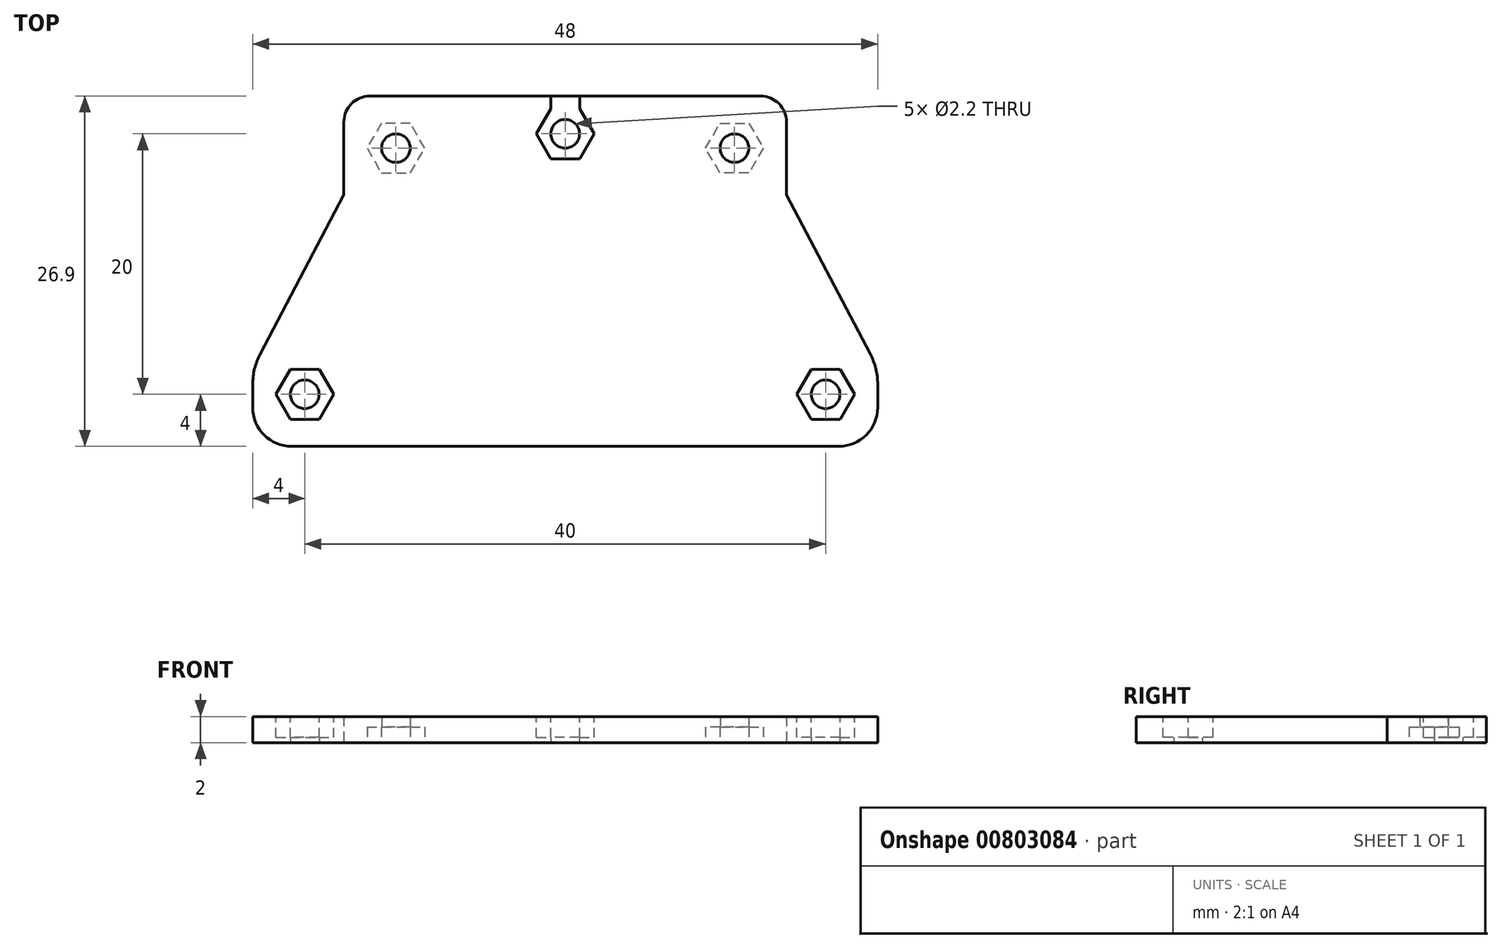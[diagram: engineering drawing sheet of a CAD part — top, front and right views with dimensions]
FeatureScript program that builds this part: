
annotation { "Feature Type Name" : "Feature", "Feature Type Description" : "" }
export const myFeature = defineFeature(function(context is Context, id is Id, definition is map)
    precondition{}
    {
        {
            var Q0;
            Q0=qCreatedBy(makeId("Top.planeOp"),FACE);
            var sketch = newSketch(context, id + "F0", { "sketchPlane" : qUnion([Q0])});
            skCircle(sketch, "E0", {"center": v(-13, 0) * mm, "radius": 1.1 * mm});
            skCircle(sketch, "E1", {"center": v(0, 1.1) * mm, "radius": 1.1 * mm});
            skCircle(sketch, "E2", {"center": v(-20, -18.9) * mm, "radius": 1.1 * mm});
            skCircle(sketch, "E3.MirrorC", {"center": v(20, -18.9) * mm, "radius": 1.1 * mm});
            skCircle(sketch, "E4.MirrorC", {"center": v(13, 0) * mm, "radius": 1.1 * mm});
            skLineSegment(sketch, "E5", {"start": v(-14.82, 3.1) * mm, "end": v(20.83, 3.1) * mm, "construction": true});
            skSolve(sketch);
        }
        {
            var Q0;
            Q0=qCreatedBy(makeId("Top.planeOp"),FACE);
            var sketch = newSketch(context, id + "F1", { "sketchPlane" : qUnion([Q0])});
            skLineSegment(sketch, "E6", {"start": v(-3, 4) * mm, "end": v(-13, 4) * mm});
            skLineSegment(sketch, "E7", {"start": v(-17, -3.6) * mm, "end": v(-24, -16.9) * mm});
            skLineSegment(sketch, "E8", {"start": v(-24, -22.9) * mm, "end": v(0, -22.9) * mm});
            skLineSegment(sketch, "E9", {"start": v(-3, 4) * mm, "end": v(0, 4) * mm});
            skLineSegment(sketch, "E10", {"start": v(-13, 4) * mm, "end": v(-17, 4) * mm});
            skLineSegment(sketch, "E11", {"start": v(-17, 4) * mm, "end": v(-17, -3.6) * mm});
            skLineSegment(sketch, "E12", {"start": v(-24, -16.9) * mm, "end": v(-24, -22.9) * mm});
            skLineSegment(sketch, "E13.MirrorCS", {"start": v(24, -22.9) * mm, "end": v(0, -22.9) * mm});
            skLineSegment(sketch, "E14.MirrorCS", {"start": v(17, -3.6) * mm, "end": v(24, -16.9) * mm});
            skLineSegment(sketch, "E15.MirrorCS", {"start": v(24, -16.9) * mm, "end": v(24, -22.9) * mm});
            skLineSegment(sketch, "E16.MirrorCS", {"start": v(3, 4) * mm, "end": v(0, 4) * mm});
            skLineSegment(sketch, "E17.MirrorCS", {"start": v(13, 4) * mm, "end": v(17, 4) * mm});
            skLineSegment(sketch, "E18.MirrorCS", {"start": v(3, 4) * mm, "end": v(13, 4) * mm});
            skLineSegment(sketch, "E19.MirrorCS", {"start": v(17, 4) * mm, "end": v(17, -3.6) * mm});
            skSolve(sketch);
        }
        {
            var Q0;
            Q0=qSketchRegion(id+"F1",true);
            extrude(context, id + "F2", {"entities" : qUnion([Q0]), "depth" : 2 * mm, "offsetDistance" : 25 * mm});
        }
        {
            var Q0;
            Q0=makeQuery(id+"F2.opExtrude","CAP_FACE",FACE,{"disambiguationData":[OSD([sQuery(id+"F1.wireOp",EDGE,"E6"),sQuery(id+"F1.wireOp",EDGE,"E7"),sQuery(id+"F1.wireOp",EDGE,"E8"),sQuery(id+"F1.wireOp",EDGE,"E9"),sQuery(id+"F1.wireOp",EDGE,"E10"),sQuery(id+"F1.wireOp",EDGE,"E11"),sQuery(id+"F1.wireOp",EDGE,"E12"),sQuery(id+"F1.wireOp",EDGE,"E13.MirrorCS"),sQuery(id+"F1.wireOp",EDGE,"E14.MirrorCS"),sQuery(id+"F1.wireOp",EDGE,"E15.MirrorCS"),sQuery(id+"F1.wireOp",EDGE,"E16.MirrorCS"),sQuery(id+"F1.wireOp",EDGE,"E17.MirrorCS"),sQuery(id+"F1.wireOp",EDGE,"E18.MirrorCS"),sQuery(id+"F1.wireOp",EDGE,"E19.MirrorCS")])],"isStart":true});
            var sketch = newSketch(context, id + "F3", { "sketchPlane" : qUnion([Q0])});
            skCircle(sketch, "E20", {"center": v(20, 18.9) * mm, "radius": 1.1 * mm});
            skCircle(sketch, "E21", {"center": v(13, 0) * mm, "radius": 1.1 * mm});
            skCircle(sketch, "E22", {"center": v(0, -1.1) * mm, "radius": 1.1 * mm});
            skCircle(sketch, "E23", {"center": v(-13, 0) * mm, "radius": 1.1 * mm});
            skCircle(sketch, "E24", {"center": v(-20, 18.9) * mm, "radius": 1.1 * mm});
            skSolve(sketch);
        }
        {
            var Q0;
            Q0=qSketchRegion(id+"F3",true);
            extrude(context, id + "F4", {"entities" : qUnion([Q0]), "operationType" : NewBodyOperationType.REMOVE, "endBound" : BoundingType.UP_TO_NEXT, "oppositeDirection" : true, "depth" : 25 * mm, "offsetDistance" : 25 * mm});
        }
        {
            var Q0;
            Q0=qCreatedBy(makeId("Top.planeOp"),FACE);
            var sketch = newSketch(context, id + "F5", { "sketchPlane" : qUnion([Q0])});
            skCircle(sketch, "E25.cCircle", {"center": v(13, 0) * mm, "radius": 1.92 * mm, "construction": true});
            skLineSegment(sketch, "E25.0", {"start": v(11.9, -1.92) * mm, "end": v(10.78, 0) * mm});
            skLineSegment(sketch, "E25.1", {"start": v(10.78, 0) * mm, "end": v(11.9, 1.92) * mm});
            skLineSegment(sketch, "E25.2", {"start": v(11.9, 1.92) * mm, "end": v(14.1, 1.92) * mm});
            skLineSegment(sketch, "E25.3", {"start": v(14.1, 1.92) * mm, "end": v(15.22, 0) * mm});
            skLineSegment(sketch, "E25.4", {"start": v(15.22, 0) * mm, "end": v(14.1, -1.92) * mm});
            skLineSegment(sketch, "E25.5", {"start": v(14.1, -1.92) * mm, "end": v(11.9, -1.92) * mm});
            skPoint(sketch, "E25.0.midPoint", {"position": v(11.34, -0.96) * mm});
            skLineSegment(sketch, "E26.MirrorCS", {"start": v(-11.9, -1.92) * mm, "end": v(-10.78, 0) * mm});
            skLineSegment(sketch, "E27.MirrorCS", {"start": v(-14.1, 1.92) * mm, "end": v(-15.22, 0) * mm});
            skPoint(sketch, "E28.MirrorP", {"position": v(-11.34, -0.96) * mm});
            skCircle(sketch, "E29.MirrorC", {"center": v(-13, 0) * mm, "radius": 1.92 * mm, "construction": true});
            skLineSegment(sketch, "E30.MirrorCS", {"start": v(-10.78, 0) * mm, "end": v(-11.9, 1.92) * mm});
            skLineSegment(sketch, "E31.MirrorCS", {"start": v(-11.9, 1.92) * mm, "end": v(-14.1, 1.92) * mm});
            skLineSegment(sketch, "E32.MirrorCS", {"start": v(-15.22, 0) * mm, "end": v(-14.1, -1.92) * mm});
            skLineSegment(sketch, "E33.MirrorCS", {"start": v(-14.1, -1.92) * mm, "end": v(-11.9, -1.92) * mm});
            skSolve(sketch);
        }
        {
            var Q0;
            Q0=qSketchRegion(id+"F5",true);
            extrude(context, id + "F6", {"entities" : qUnion([Q0]), "operationType" : NewBodyOperationType.REMOVE, "depth" : 1.2 * mm, "offsetDistance" : 25 * mm});
        }
        {
            var Q0;
            Q0=makeQuery(id+"F2.opExtrude","CAP_FACE",FACE,{"disambiguationData":[OSD([sQuery(id+"F1.wireOp",EDGE,"E6"),sQuery(id+"F1.wireOp",EDGE,"E7"),sQuery(id+"F1.wireOp",EDGE,"E8"),sQuery(id+"F1.wireOp",EDGE,"E9"),sQuery(id+"F1.wireOp",EDGE,"E10"),sQuery(id+"F1.wireOp",EDGE,"E11"),sQuery(id+"F1.wireOp",EDGE,"E12"),sQuery(id+"F1.wireOp",EDGE,"E13.MirrorCS"),sQuery(id+"F1.wireOp",EDGE,"E14.MirrorCS"),sQuery(id+"F1.wireOp",EDGE,"E15.MirrorCS"),sQuery(id+"F1.wireOp",EDGE,"E16.MirrorCS"),sQuery(id+"F1.wireOp",EDGE,"E17.MirrorCS"),sQuery(id+"F1.wireOp",EDGE,"E18.MirrorCS"),sQuery(id+"F1.wireOp",EDGE,"E19.MirrorCS")])],"isStart":false});
            var sketch = newSketch(context, id + "F7", { "sketchPlane" : qUnion([Q0])});
            skCircle(sketch, "E34.cCircle", {"center": v(-20, -18.9) * mm, "radius": 1.92 * mm, "construction": true});
            skLineSegment(sketch, "E34.0", {"start": v(-18.9, -16.98) * mm, "end": v(-17.78, -18.9) * mm});
            skLineSegment(sketch, "E34.1", {"start": v(-17.78, -18.9) * mm, "end": v(-18.9, -20.82) * mm});
            skLineSegment(sketch, "E34.2", {"start": v(-18.9, -20.82) * mm, "end": v(-21.1, -20.82) * mm});
            skLineSegment(sketch, "E34.3", {"start": v(-21.1, -20.82) * mm, "end": v(-22.22, -18.9) * mm});
            skLineSegment(sketch, "E34.4", {"start": v(-22.22, -18.9) * mm, "end": v(-21.1, -16.98) * mm});
            skLineSegment(sketch, "E34.5", {"start": v(-21.1, -16.98) * mm, "end": v(-18.9, -16.98) * mm});
            skPoint(sketch, "E34.0.midPoint", {"position": v(-18.34, -17.94) * mm});
            skCircle(sketch, "E35.cCircle", {"center": v(0, 1.1) * mm, "radius": 1.92 * mm, "construction": true});
            skLineSegment(sketch, "E35.0", {"start": v(-1.1, 3.02) * mm, "end": v(1.1, 3.02) * mm});
            skLineSegment(sketch, "E35.1", {"start": v(1.1, 3.02) * mm, "end": v(2.22, 1.1) * mm});
            skLineSegment(sketch, "E35.2", {"start": v(2.22, 1.1) * mm, "end": v(1.1, -0.82) * mm});
            skLineSegment(sketch, "E35.3", {"start": v(1.1, -0.82) * mm, "end": v(-1.1, -0.82) * mm});
            skLineSegment(sketch, "E35.4", {"start": v(-1.1, -0.82) * mm, "end": v(-2.22, 1.1) * mm});
            skLineSegment(sketch, "E35.5", {"start": v(-2.22, 1.1) * mm, "end": v(-1.1, 3.02) * mm});
            skPoint(sketch, "E35.0.midPoint", {"position": v(0, 3.02) * mm});
            skLineSegment(sketch, "E36.MirrorCS", {"start": v(17.78, -18.9) * mm, "end": v(18.9, -20.82) * mm});
            skLineSegment(sketch, "E37.MirrorCS", {"start": v(22.22, -18.9) * mm, "end": v(21.1, -16.98) * mm});
            skLineSegment(sketch, "E38.MirrorCS", {"start": v(18.9, -16.98) * mm, "end": v(17.78, -18.9) * mm});
            skLineSegment(sketch, "E39.MirrorCS", {"start": v(21.1, -20.82) * mm, "end": v(22.22, -18.9) * mm});
            skLineSegment(sketch, "E40.MirrorCS", {"start": v(21.1, -16.98) * mm, "end": v(18.9, -16.98) * mm});
            skCircle(sketch, "E41.MirrorC", {"center": v(20, -18.9) * mm, "radius": 1.92 * mm, "construction": true});
            skLineSegment(sketch, "E42.MirrorCS", {"start": v(18.9, -20.82) * mm, "end": v(21.1, -20.82) * mm});
            skPoint(sketch, "E43.MirrorP", {"position": v(18.34, -17.94) * mm});
            skLineSegment(sketch, "E44", {"start": v(-1.1, 3.02) * mm, "end": v(-1.1, 4) * mm});
            skLineSegment(sketch, "E45", {"start": v(-1.1, 4) * mm, "end": v(1.1, 4) * mm});
            skLineSegment(sketch, "E46", {"start": v(1.1, 4) * mm, "end": v(1.1, 3.02) * mm});
            skSolve(sketch);
        }
        {
            var Q0;
            Q0=qSketchRegion(id+"F7",true);
            var Q1;
            Q1=qConstructionFilter(qBodyType(qCreatedBy(id+"F7",EDGE),BodyType.WIRE),ConstructionObject.NO);
            extrude(context, id + "F8", {"entities" : qUnion([Q0]), "operationType" : NewBodyOperationType.REMOVE, "surfaceEntities" : qUnion([Q1]), "oppositeDirection" : true, "depth" : 1.6 * mm, "offsetDistance" : 25 * mm});
        }
        {
            var Q0;
            Q0=makeQuery(id+"F2.opExtrude","SWEPT_EDGE",EDGE,{"disambiguationData":[OSD([sQuery(id+"F1.wireOp",EDGE,"E10"),sQuery(id+"F1.wireOp",EDGE,"E11")])]});
            var Q1;
            Q1=makeQuery(id+"F2.opExtrude","SWEPT_EDGE",EDGE,{"disambiguationData":[OSD([sQuery(id+"F1.wireOp",EDGE,"E17.MirrorCS"),sQuery(id+"F1.wireOp",EDGE,"E19.MirrorCS")])]});
            fillet(context, id + "F9", {"entities" : qUnion([Q0, Q1]), "radius" : 2 * mm, "tangentPropagation" : true, "allowEdgeOverflow" : false});
        }
        {
            var Q0;
            Q0=makeQuery(id+"F2.opExtrude","SWEPT_EDGE",EDGE,{"disambiguationData":[OSD([sQuery(id+"F1.wireOp",EDGE,"E14.MirrorCS"),sQuery(id+"F1.wireOp",EDGE,"E15.MirrorCS")])]});
            var Q1;
            Q1=makeQuery(id+"F2.opExtrude","SWEPT_EDGE",EDGE,{"disambiguationData":[OSD([sQuery(id+"F1.wireOp",EDGE,"E7"),sQuery(id+"F1.wireOp",EDGE,"E12")])]});
            var Q2;
            Q2=makeQuery(id+"F2.opExtrude","SWEPT_EDGE",EDGE,{"disambiguationData":[OSD([sQuery(id+"F1.wireOp",EDGE,"E6"),sQuery(id+"F1.wireOp",EDGE,"E9")])]});
            var Q3;
            Q3=makeQuery(id+"F2.opExtrude","SWEPT_EDGE",EDGE,{"disambiguationData":[OSD([sQuery(id+"F1.wireOp",EDGE,"E16.MirrorCS"),sQuery(id+"F1.wireOp",EDGE,"E18.MirrorCS")])]});
            fillet(context, id + "F10", {"entities" : qUnion([Q0, Q1, Q2, Q3]), "radius" : 5 * mm, "tangentPropagation" : true, "allowEdgeOverflow" : false});
        }
        {
            var Q0;
            Q0=makeQuery(id+"F2.opExtrude","SWEPT_EDGE",EDGE,{"disambiguationData":[OSD([sQuery(id+"F1.wireOp",EDGE,"E13.MirrorCS"),sQuery(id+"F1.wireOp",EDGE,"E15.MirrorCS")])]});
            var Q1;
            Q1=makeQuery(id+"F2.opExtrude","SWEPT_EDGE",EDGE,{"disambiguationData":[OSD([sQuery(id+"F1.wireOp",EDGE,"E8"),sQuery(id+"F1.wireOp",EDGE,"E12")])]});
            fillet(context, id + "F11", {"entities" : qUnion([Q0, Q1]), "radius" : 3 * mm, "tangentPropagation" : true, "allowEdgeOverflow" : false});
        }
    });
